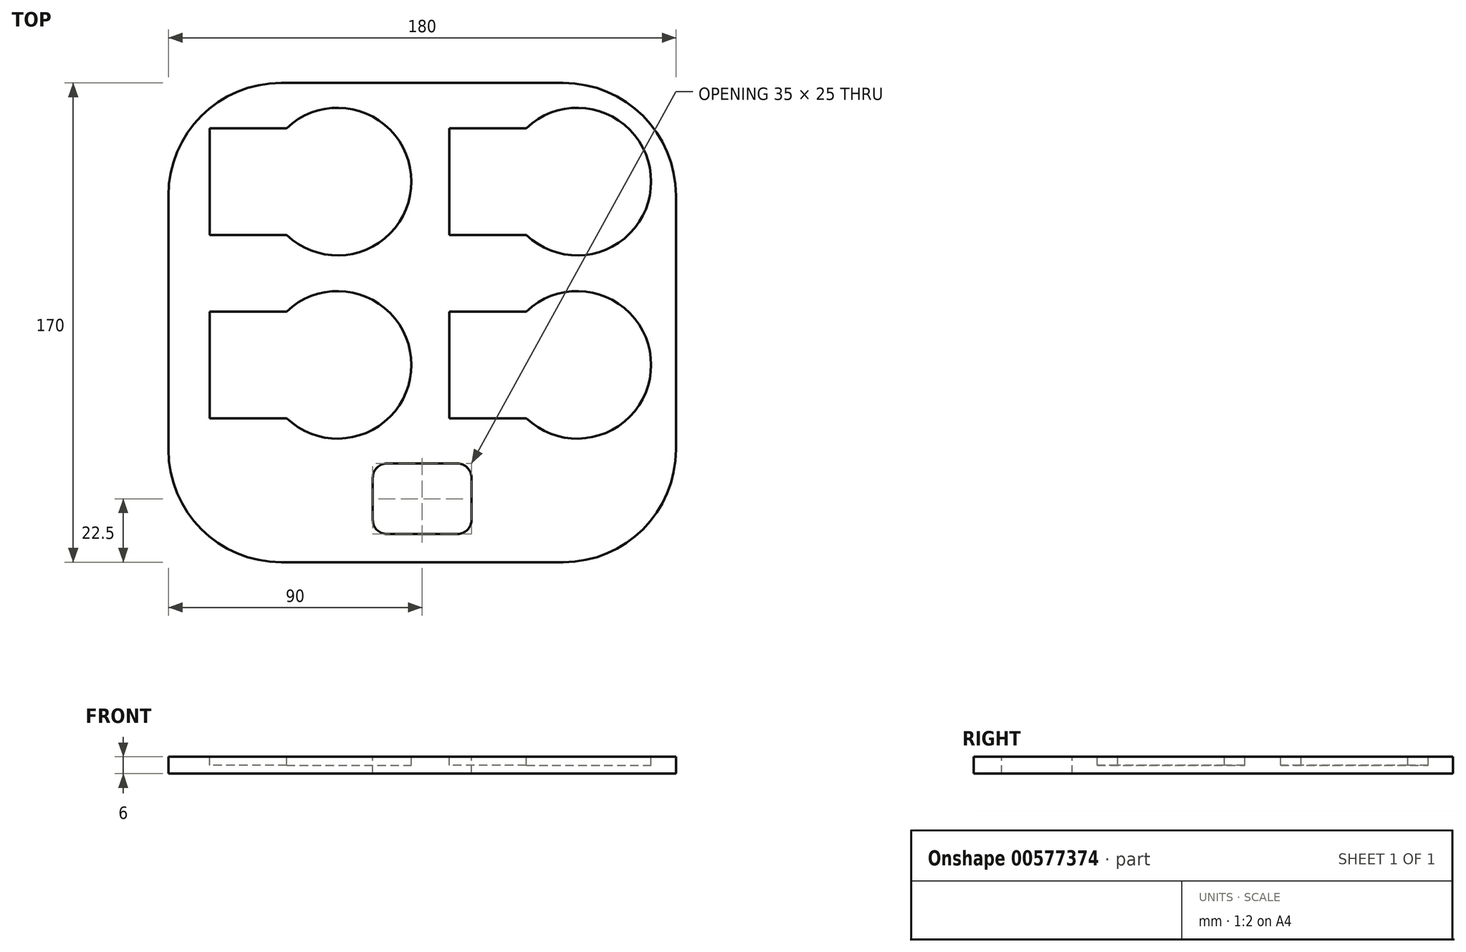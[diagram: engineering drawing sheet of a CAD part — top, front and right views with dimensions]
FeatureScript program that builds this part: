
annotation { "Feature Type Name" : "Feature", "Feature Type Description" : "" }
export const myFeature = defineFeature(function(context is Context, id is Id, definition is map)
    precondition{}
    {
        {
            var Q0;
            Q0=qCreatedBy(makeId("Top.planeOp"),FACE);
            var sketch = newSketch(context, id + "F0", { "sketchPlane" : qUnion([Q0])});
            skLineSegment(sketch, "E0.bottom", {"start": v(-50, 85) * mm, "end": v(50, 85) * mm});
            skLineSegment(sketch, "E0.top", {"start": v(-50, -85) * mm, "end": v(50, -85) * mm});
            skLineSegment(sketch, "E0.left", {"start": v(-90, 45) * mm, "end": v(-90, -45) * mm});
            skLineSegment(sketch, "E0.right", {"start": v(90, 45) * mm, "end": v(90, -45) * mm});
            skLineSegment(sketch, "E1", {"start": v(0, 0) * mm, "end": v(90, 0) * mm});
            skLineSegment(sketch, "E2", {"start": v(0, 0) * mm, "end": v(0, 85) * mm});
            skPoint(sketch, "E3.visualSharp", {"position": v(-90, 85) * mm});
            skArc(sketch, "E3.filletArc", {"start": v(-50, 85) * mm, "mid": v(-78.28, 73.28) * mm, "end": v(-90, 45) * mm});
            skPoint(sketch, "E4.visualSharp", {"position": v(90, 85) * mm});
            skArc(sketch, "E4.filletArc", {"start": v(90, 45) * mm, "mid": v(78.28, 73.28) * mm, "end": v(50, 85) * mm});
            skPoint(sketch, "E5.visualSharp", {"position": v(90, -85) * mm});
            skArc(sketch, "E5.filletArc", {"start": v(50, -85) * mm, "mid": v(78.28, -73.28) * mm, "end": v(90, -45) * mm});
            skPoint(sketch, "E6.visualSharp", {"position": v(-90, -85) * mm});
            skArc(sketch, "E6.filletArc", {"start": v(-90, -45) * mm, "mid": v(-78.28, -73.28) * mm, "end": v(-50, -85) * mm});
            skSolve(sketch);
        }
        {
            var Q0;
            {var subQ1=sQuery(id+"F0.wireOp",EDGE,"E0.top");Q0=makeQuery(id+"F0.imprint","IMPRINT",FACE,{"disambiguationData":[TD([[makeQuery(id+"F0.imprint","IMPRINT",EDGE,{"derivedFrom":subQ1}),1.0]])]});}
            var Q1;
            {var subQ4=sQuery(id+"F0.wireOp",EDGE,"E1");Q1=makeQuery(id+"F0.imprint","IMPRINT",FACE,{"disambiguationData":[TD([[makeQuery(id+"F0.imprint","IMPRINT",EDGE,{"derivedFrom":subQ4}),1.0]])]});}
            extrude(context, id + "F1", {"entities" : qUnion([Q0, Q1]), "depth" : 6 * mm, "offsetDistance" : 25.4 * mm});
        }
        {
            var Q0;
            Q0=makeQuery(id+"F1.opExtrude","CAP_FACE",FACE,{"disambiguationData":[OSD([sQuery(id+"F0.wireOp",EDGE,"E0.bottom"),sQuery(id+"F0.wireOp",EDGE,"E0.top"),sQuery(id+"F0.wireOp",EDGE,"E0.left"),sQuery(id+"F0.wireOp",EDGE,"E0.right")])],"isStart":false});
            var sketch = newSketch(context, id + "F2", { "sketchPlane" : qUnion([Q0])});
            skArc(sketch, "E7", {"start": v(-45.94, 36.06) * mm, "mid": v(-8.82, 50) * mm, "end": v(-45.94, 63.94) * mm});
            skLineSegment(sketch, "E8.bottom", {"start": v(-45.94, 63.94) * mm, "end": v(-70.38, 63.94) * mm});
            skLineSegment(sketch, "E8.top", {"start": v(-45.94, 36.06) * mm, "end": v(-70.38, 36.06) * mm});
            skLineSegment(sketch, "E8.right", {"start": v(-70.38, 63.94) * mm, "end": v(-70.38, 36.06) * mm});
            skPoint(sketch, "E9.orphan", {"position": v(-30, 63.94) * mm});
            skPoint(sketch, "E10.orphan", {"position": v(-30, 36.06) * mm});
            skArc(sketch, "E11.0", {"start": v(-48.07, 31.06) * mm, "mid": v(-3.82, 50) * mm, "end": v(-48.07, 68.94) * mm});
            skLineSegment(sketch, "E11.1", {"start": v(-48.07, 31.06) * mm, "end": v(-75.38, 31.06) * mm});
            skLineSegment(sketch, "E11.2", {"start": v(-75.38, 68.94) * mm, "end": v(-75.38, 31.06) * mm});
            skLineSegment(sketch, "E11.3", {"start": v(-48.07, 68.94) * mm, "end": v(-75.38, 68.94) * mm});
            skArc(sketch, "E12.0.1.0", {"start": v(-48.07, -33.94) * mm, "mid": v(-3.82, -15) * mm, "end": v(-48.07, 3.94) * mm});
            skLineSegment(sketch, "E12.0.1.1", {"start": v(-48.07, 3.94) * mm, "end": v(-75.38, 3.94) * mm});
            skLineSegment(sketch, "E12.0.1.2", {"start": v(-75.38, 3.94) * mm, "end": v(-75.38, -33.94) * mm});
            skLineSegment(sketch, "E12.0.1.3", {"start": v(-48.07, -33.94) * mm, "end": v(-75.38, -33.94) * mm});
            skArc(sketch, "E12.1.0.0", {"start": v(36.93, 31.06) * mm, "mid": v(81.18, 50) * mm, "end": v(36.93, 68.94) * mm});
            skLineSegment(sketch, "E12.1.0.1", {"start": v(36.93, 68.94) * mm, "end": v(9.63, 68.94) * mm});
            skLineSegment(sketch, "E12.1.0.2", {"start": v(9.63, 68.94) * mm, "end": v(9.63, 31.06) * mm});
            skLineSegment(sketch, "E12.1.0.3", {"start": v(36.93, 31.06) * mm, "end": v(9.63, 31.06) * mm});
            skArc(sketch, "E12.1.1.0", {"start": v(36.93, -33.94) * mm, "mid": v(81.18, -15) * mm, "end": v(36.93, 3.94) * mm});
            skLineSegment(sketch, "E12.1.1.1", {"start": v(36.93, 3.94) * mm, "end": v(9.63, 3.94) * mm});
            skLineSegment(sketch, "E12.1.1.2", {"start": v(9.63, 3.94) * mm, "end": v(9.63, -33.94) * mm});
            skLineSegment(sketch, "E12.1.1.3", {"start": v(36.93, -33.94) * mm, "end": v(9.63, -33.94) * mm});
            skLineSegment(sketch, "E12.direction1", {"start": v(-48.07, 31.06) * mm, "end": v(36.93, 31.06) * mm, "construction": true});
            skLineSegment(sketch, "E12.direction2", {"start": v(-48.07, 31.06) * mm, "end": v(-48.07, -33.94) * mm, "construction": true});
            skLineSegment(sketch, "E13.bottom", {"start": v(12.5, -45) * mm, "end": v(-12.5, -45) * mm});
            skLineSegment(sketch, "E13.top", {"start": v(12.5, -70) * mm, "end": v(-12.5, -70) * mm});
            skLineSegment(sketch, "E13.left", {"start": v(17.5, -50) * mm, "end": v(17.5, -65) * mm});
            skLineSegment(sketch, "E13.right", {"start": v(-17.5, -50) * mm, "end": v(-17.5, -65) * mm});
            skPoint(sketch, "E14.visualSharp", {"position": v(-17.5, -45) * mm});
            skArc(sketch, "E14.filletArc", {"start": v(-12.5, -45) * mm, "mid": v(-16.04, -46.46) * mm, "end": v(-17.5, -50) * mm});
            skPoint(sketch, "E15.visualSharp", {"position": v(17.5, -45) * mm});
            skArc(sketch, "E15.filletArc", {"start": v(17.5, -50) * mm, "mid": v(16.04, -46.46) * mm, "end": v(12.5, -45) * mm});
            skPoint(sketch, "E16.visualSharp", {"position": v(17.5, -70) * mm});
            skArc(sketch, "E16.filletArc", {"start": v(12.5, -70) * mm, "mid": v(16.04, -68.54) * mm, "end": v(17.5, -65) * mm});
            skPoint(sketch, "E17.visualSharp", {"position": v(-17.5, -70) * mm});
            skArc(sketch, "E17.filletArc", {"start": v(-17.5, -65) * mm, "mid": v(-16.04, -68.54) * mm, "end": v(-12.5, -70) * mm});
            skSolve(sketch);
        }
        {
            var Q0;
            Q0=makeQuery(id+"F2.imprint","IMPRINT",FACE,{"disambiguationData":[TD([[makeQuery(id+"F2.imprint","IMPRINT",EDGE,{"derivedFrom":sQuery(id+"F2.wireOp",EDGE,"E7")}),-1.0]])]});
            var Q1;
            Q1=makeQuery(id+"F2.imprint","IMPRINT",FACE,{"disambiguationData":[TD([[makeQuery(id+"F2.imprint","IMPRINT",EDGE,{"derivedFrom":sQuery(id+"F2.wireOp",EDGE,"E12.1.0.0")}),1.0]])]});
            var Q2;
            Q2=makeQuery(id+"F2.imprint","IMPRINT",FACE,{"disambiguationData":[TD([[makeQuery(id+"F2.imprint","IMPRINT",EDGE,{"derivedFrom":sQuery(id+"F2.wireOp",EDGE,"E12.1.1.0")}),1.0]])]});
            var Q3;
            Q3=makeQuery(id+"F2.imprint","IMPRINT",FACE,{"disambiguationData":[TD([[makeQuery(id+"F2.imprint","IMPRINT",EDGE,{"derivedFrom":sQuery(id+"F2.wireOp",EDGE,"E12.0.1.0")}),1.0]])]});
            var Q4;
            Q4=makeQuery(id+"F2.imprint","IMPRINT",FACE,{"disambiguationData":[TD([[makeQuery(id+"F2.imprint","IMPRINT",EDGE,{"derivedFrom":sQuery(id+"F2.wireOp",EDGE,"E7")}),1.0]])]});
            extrude(context, id + "F3", {"entities" : qUnion([Q0, Q1, Q2, Q3, Q4]), "operationType" : NewBodyOperationType.REMOVE, "oppositeDirection" : true, "depth" : 3 * mm, "offsetDistance" : 25 * mm});
        }
        {
            var Q0;
            Q0=makeQuery(id+"F1.opExtrude","CAP_FACE",FACE,{"disambiguationData":[OSD([sQuery(id+"F0.wireOp",EDGE,"E0.bottom"),sQuery(id+"F0.wireOp",EDGE,"E0.top"),sQuery(id+"F0.wireOp",EDGE,"E0.left"),sQuery(id+"F0.wireOp",EDGE,"E0.right")])],"isStart":false});
            var sketch = newSketch(context, id + "F4", { "sketchPlane" : qUnion([Q0])});
            skLineSegment(sketch, "E18.bottom", {"start": v(12.5, -50) * mm, "end": v(-12.5, -50) * mm});
            skLineSegment(sketch, "E18.top", {"start": v(12.5, -75) * mm, "end": v(-12.5, -75) * mm});
            skLineSegment(sketch, "E18.left", {"start": v(17.5, -55) * mm, "end": v(17.5, -70) * mm});
            skLineSegment(sketch, "E18.right", {"start": v(-17.5, -55) * mm, "end": v(-17.5, -70) * mm});
            skArc(sketch, "E19.filletArc", {"start": v(-12.5, -50) * mm, "mid": v(-16.04, -51.46) * mm, "end": v(-17.5, -55) * mm});
            skArc(sketch, "E20.filletArc", {"start": v(17.5, -55) * mm, "mid": v(16.04, -51.46) * mm, "end": v(12.5, -50) * mm});
            skPoint(sketch, "E21.visualSharp", {"position": v(17.5, -75) * mm});
            skArc(sketch, "E21.filletArc", {"start": v(12.5, -75) * mm, "mid": v(16.04, -73.54) * mm, "end": v(17.5, -70) * mm});
            skPoint(sketch, "E22.visualSharp", {"position": v(-17.5, -75) * mm});
            skArc(sketch, "E22.filletArc", {"start": v(-17.5, -70) * mm, "mid": v(-16.04, -73.54) * mm, "end": v(-12.5, -75) * mm});
            skSolve(sketch);
        }
        {
            var Q0;
            Q0 = qSketchRegion(id + "F4", true);
            extrude(context, id + "F5", {"entities" : qUnion([Q0]), "operationType" : NewBodyOperationType.REMOVE, "oppositeDirection" : true, "depth" : 25 * mm, "offsetDistance" : 25 * mm});
        }
    });
